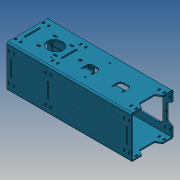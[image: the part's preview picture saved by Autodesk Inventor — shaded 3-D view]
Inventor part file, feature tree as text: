
AUTODESK INVENTOR PART (.ipt)
format: ipt  version: 2017 (Build 210142000, 142)  size: 1,324,032 bytes
history: native  units: mm
features: other x17, sketch x5, extrude x3, projected_geometry x3, plane x1, mirror x1
ambient origin geometry x8: Origin, YZ Plane, XZ Plane, XY Plane, X Axis, Y Axis, Z Axis, Center Point
bodies: Body1 (feature_tree)
feature tree (30):
  other  "Sólido1"
  sketch  "Boceto1"  dims[d1=56.4mm d2=72.0mm]
  extrude  "Extrusión1"  Depth=72.0mm
  other  "Pestaña1"
  other  "Pliegue1"
  other  "Pliegue2"
  sketch  "Boceto4"  dims[d6=8.0mm d8=5.0mm]
  other  "Cara1"
  other  "Cara2"
  extrude  "Extrusión4"  Depth=42.0mm
  sketch  "Boceto5"  dims[d9=41.14mm]
  other  "Cara3"
  plane  "Plano de trabajo1"
  mirror  "Simetría1"
  extrude  "Extrusión5"  Depth=5.0mm
  sketch  "Boceto2"  dims[d4=200.0mm d5=42.0mm]
  other  "Placa1"
  other  "Doblez1"
  other  "Esquina1"
  other  "Placa2"
  other  "Doblez2"
  other  "Placa3"
  other  "Doblez3"
  other  "Placa4"
  other  "Doblez4"
  sketch  "Boceto6"  dims[d10=6.0mm d11=53.14mm d12=6.0mm d13=4.0mm d14=100.0mm d15=20.0mm d16=70.0mm d17=60.0mm d18=4.0mm d19=33.93mm d20=22.0mm d21=120.0mm d22=130.0mm d23=20.0mm d24=4.0mm d25=0.0mm d26=4.0mm d27=2.0mm d28=8.0mm d29=4.0mm d30=120.0mm d31=90.0deg d32=0.1mm d33=16.0mm d34=4.0mm d35=4.0mm d42=47.14mm d43=47.14mm d44=20.0mm d45=6.0mm d46=14.2mm d47=25.0mm d48=0.1mm d49=4.0mm d50=2.0mm d51=8.0mm d52=4.0mm d53=0.1mm d54=4.0mm d55=2.0mm d56=8.0mm d57=4.0mm d58=0.5mm d59=0.5mm d60=20.0mm d61=24.0mm d62=4.4mm d63=41.0mm d70=4.4mm d71=130.8mm d72=25.0mm d73=0.1mm d74=4.0mm d75=2.0mm d76=8.0mm d77=4.0mm d86=50.0mm d87=355.0mm d88=12.5mm d89=12.5mm d90=23.6mm d91=11.8mm d97=190.1mm d102=12.0mm d103=0.25mm d109=12.5mm d113=10.0mm d114=0.0mm d115=10.0mm d116=0.0mm d118=4.0mm d119=5.0mm d120=3.0mm d121=4.0mm d122=5.0mm d123=12.0mm d124=6.0mm d125=24.0mm d126=120.0mm d128=4.0mm d129=2.0mm d130=8.0mm d131=4.0mm d132=90.0deg d133=1.0mm d134=4.0mm d135=2.0mm d136=8.0mm d137=4.0mm d138=90.0deg d139=0.1mm d140=5.0mm d141=90.0mm d142=10.0mm d143=4.0mm d144=80.0mm d145=5.0mm d146=60.0deg d147=55.0mm d148=10.4mm d149=10.4mm d150=4.0mm d151=80.0mm d152=105.5mm d153=10.0mm d154=5.0mm d155=60.0deg d156=41.0mm d157=4.2mm d158=12.5mm]
  projected_geometry  "Contorno proyectado2"
  projected_geometry  "Contorno proyectado3"
  projected_geometry  "Contorno proyectado4"
  other  "Definición1"
